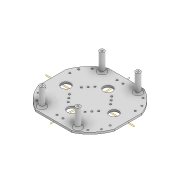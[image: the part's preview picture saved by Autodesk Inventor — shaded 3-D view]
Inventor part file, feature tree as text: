
AUTODESK INVENTOR PART (.ipt)
format: ipt  version: 2022 (Build 260153000, 153)  size: 256,512 bytes
history: native  units: mm
features: extrude x5, mirror x3, plane x2, sketch x2, fillet x1, projected_geometry x1
ambient origin geometry x8: Origin, YZ Plane, XZ Plane, XY Plane, X Axis, Y Axis, Z Axis, Center Point
bodies: Solid1 (feature_tree)
feature tree (14):
  extrude  "Extrusion1"  Depth=3.0mm TaperAngle=0.0deg
  extrude  "Extrusion3"  Depth=3.0mm
  plane  "Work Plane5"
  plane  "Work Plane6"
  mirror  "Mirror3"
  mirror  "Mirror4"
  extrude  "Extrusion4"  Depth=3.0mm
  mirror  "Mirror5"
  sketch  "Sketch9"  dims[d25=60.0mm d27=8.726646mm d28=3.0mm d30=3.0mm d32=25.0mm d33=62.0mm d34=8.0mm d35=8.0mm d36=10.0mm d37=0.0mm d38=63.0mm d39=63.0mm d40=3.0mm d41=25.0mm d42=3.0mm d43=3.0mm d44=10.0mm d45=10.0mm d46=4.95mm d47=4.95mm d48=100.0mm d49=0.0mm d50=3.0mm d51=10.0mm d52=15.0mm d53=40.0mm d54=15.0mm d55=30.0mm d56=8.0mm d57=8.0mm d58=8.0mm d59=8.0mm d60=0.1mm d61=0.1mm d62=0.1mm d63=0.1mm d64=10.0mm d65=0.0mm d66=30.0mm d67=0.0mm d68=3.0mm]
  extrude  "Extrusion5"  Depth=3.0mm
  extrude  "Extrusion6"  Depth=3.0mm
  fillet  "Fillet2"  Radius=62.0mm
  sketch  "Sketch7"  dims[d0=120.0mm d2=3.0mm d3=0.0mm]
  projected_geometry  "Projected Loop5"
